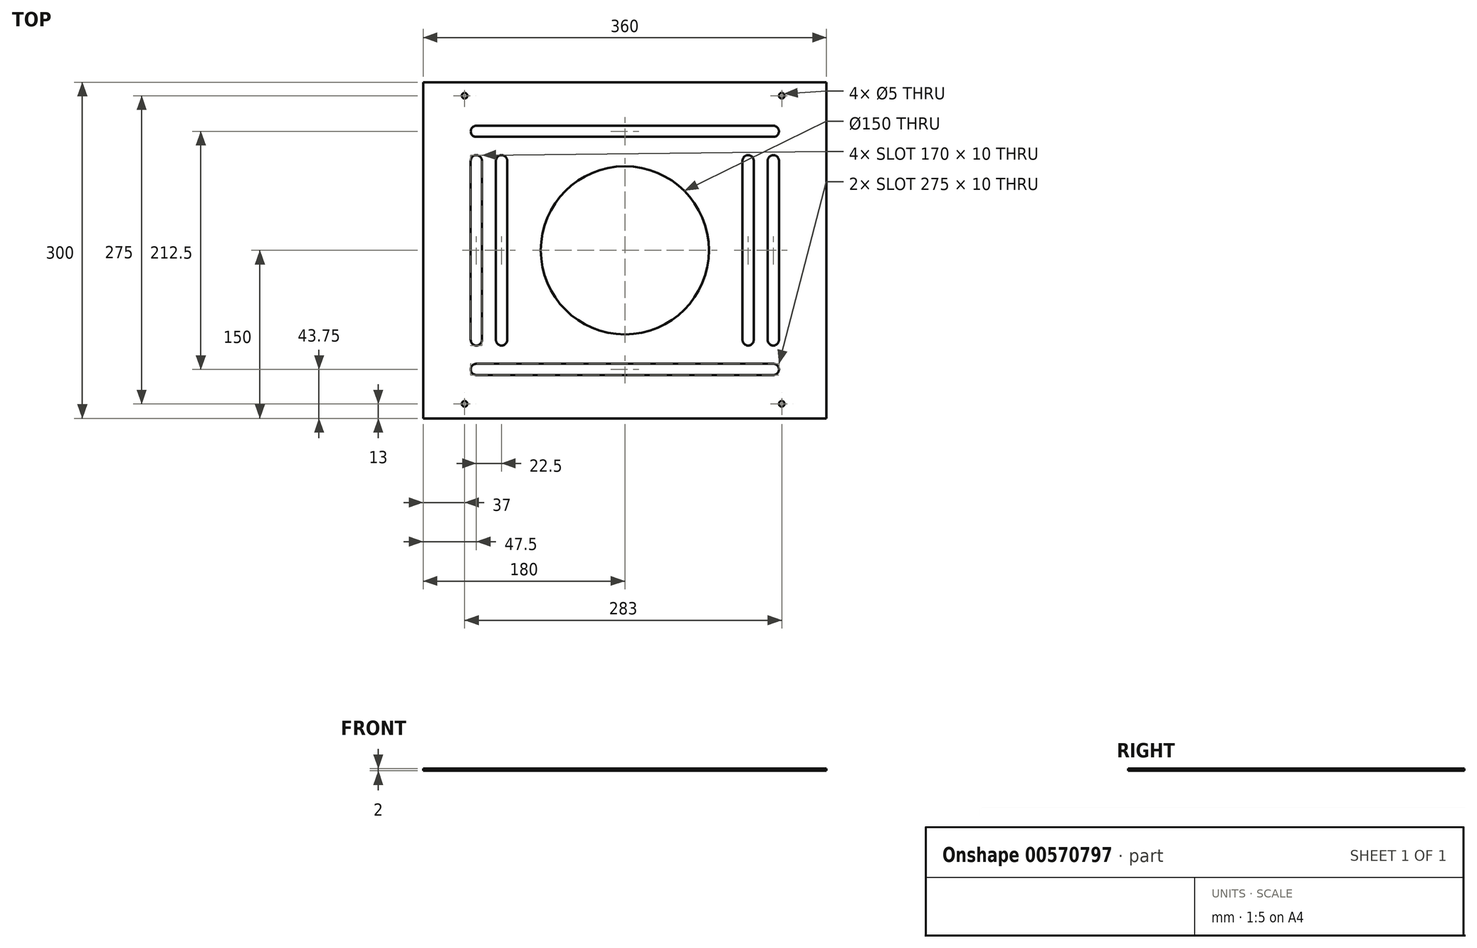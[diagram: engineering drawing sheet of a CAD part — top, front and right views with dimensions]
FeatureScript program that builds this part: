
annotation { "Feature Type Name" : "Feature", "Feature Type Description" : "" }
export const myFeature = defineFeature(function(context is Context, id is Id, definition is map)
    precondition{}
    {
        {
            var Q0;
            Q0=qCreatedBy(makeId("Top.planeOp"),FACE);
            var sketch = newSketch(context, id + "F0", { "sketchPlane" : qUnion([Q0])});
            skLineSegment(sketch, "E0.bottom", {"start": v(0, 0) * mm, "end": v(360, 0) * mm});
            skLineSegment(sketch, "E0.top", {"start": v(0, 300) * mm, "end": v(360, 300) * mm});
            skLineSegment(sketch, "E0.left", {"start": v(0, 0) * mm, "end": v(0, 300) * mm});
            skLineSegment(sketch, "E0.right", {"start": v(360, 0) * mm, "end": v(360, 300) * mm});
            skCircle(sketch, "E1", {"center": v(180, 150) * mm, "radius": 75 * mm});
            skPoint(sketch, "E1.centerSnap0", {"position": v(180, 0) * mm});
            skPoint(sketch, "E1.centerSnap1", {"position": v(0, 150) * mm});
            skCircle(sketch, "E2", {"center": v(320, 13) * mm, "radius": 2.5 * mm});
            skCircle(sketch, "E3", {"center": v(37, 13) * mm, "radius": 2.5 * mm});
            skCircle(sketch, "E4", {"center": v(37, 288) * mm, "radius": 2.5 * mm});
            skLineSegment(sketch, "E5.0", {"start": v(25, 275) * mm, "end": v(335, 275) * mm, "construction": true});
            skLineSegment(sketch, "E5.1", {"start": v(25, 25) * mm, "end": v(25, 275) * mm, "construction": true});
            skLineSegment(sketch, "E5.2", {"start": v(25, 25) * mm, "end": v(335, 25) * mm, "construction": true});
            skLineSegment(sketch, "E5.3", {"start": v(335, 25) * mm, "end": v(335, 275) * mm, "construction": true});
            skCircle(sketch, "E6", {"center": v(180, 150) * mm, "radius": 87.5 * mm, "construction": true});
            skLineSegment(sketch, "E7", {"start": v(70, 230) * mm, "end": v(70, 70) * mm, "construction": true});
            skLineSegment(sketch, "E8", {"start": v(0, 150) * mm, "end": v(360, 150) * mm, "construction": true});
            skLineSegment(sketch, "E9", {"start": v(180, 300) * mm, "end": v(180, 0) * mm, "construction": true});
            skLineSegment(sketch, "E10", {"start": v(47.5, 230) * mm, "end": v(47.5, 70) * mm, "construction": true});
            skLineSegment(sketch, "E11", {"start": v(290, 230) * mm, "end": v(290, 70) * mm, "construction": true});
            skLineSegment(sketch, "E12", {"start": v(312.5, 230) * mm, "end": v(312.5, 70) * mm, "construction": true});
            skLineSegment(sketch, "E13", {"start": v(47.5, 256.25) * mm, "end": v(312.5, 256.25) * mm, "construction": true});
            skLineSegment(sketch, "E14", {"start": v(47.5, 43.75) * mm, "end": v(312.5, 43.75) * mm, "construction": true});
            skArc(sketch, "E15.0.startCap", {"start": v(42.5, 230) * mm, "mid": v(47.5, 235) * mm, "end": v(52.5, 230) * mm});
            skArc(sketch, "E15.0.endCap", {"start": v(52.5, 70) * mm, "mid": v(47.5, 65) * mm, "end": v(42.5, 70) * mm});
            skLineSegment(sketch, "E15.0.left", {"start": v(52.5, 230) * mm, "end": v(52.5, 70) * mm});
            skLineSegment(sketch, "E15.0.right", {"start": v(42.5, 230) * mm, "end": v(42.5, 70) * mm});
            skArc(sketch, "E15.1.startCap", {"start": v(65, 230) * mm, "mid": v(70, 235) * mm, "end": v(75, 230) * mm});
            skArc(sketch, "E15.1.endCap", {"start": v(75, 70) * mm, "mid": v(70, 65) * mm, "end": v(65, 70) * mm});
            skLineSegment(sketch, "E15.1.left", {"start": v(75, 230) * mm, "end": v(75, 70) * mm});
            skLineSegment(sketch, "E15.1.right", {"start": v(65, 230) * mm, "end": v(65, 70) * mm});
            skArc(sketch, "E15.2.startCap", {"start": v(47.5, 38.75) * mm, "mid": v(42.5, 43.75) * mm, "end": v(47.5, 48.75) * mm});
            skArc(sketch, "E15.2.endCap", {"start": v(312.5, 48.75) * mm, "mid": v(317.5, 43.75) * mm, "end": v(312.5, 38.75) * mm});
            skLineSegment(sketch, "E15.2.left", {"start": v(47.5, 48.75) * mm, "end": v(312.5, 48.75) * mm});
            skLineSegment(sketch, "E15.2.right", {"start": v(47.5, 38.75) * mm, "end": v(312.5, 38.75) * mm});
            skArc(sketch, "E15.3.startCap", {"start": v(47.5, 251.25) * mm, "mid": v(42.5, 256.25) * mm, "end": v(47.5, 261.25) * mm});
            skArc(sketch, "E15.3.endCap", {"start": v(312.5, 261.25) * mm, "mid": v(317.5, 256.25) * mm, "end": v(312.5, 251.25) * mm});
            skLineSegment(sketch, "E15.3.left", {"start": v(47.5, 261.25) * mm, "end": v(312.5, 261.25) * mm});
            skLineSegment(sketch, "E15.3.right", {"start": v(47.5, 251.25) * mm, "end": v(312.5, 251.25) * mm});
            skArc(sketch, "E15.4.startCap", {"start": v(285, 230) * mm, "mid": v(290, 235) * mm, "end": v(295, 230) * mm});
            skArc(sketch, "E15.4.endCap", {"start": v(295, 70) * mm, "mid": v(290, 65) * mm, "end": v(285, 70) * mm});
            skLineSegment(sketch, "E15.4.left", {"start": v(295, 230) * mm, "end": v(295, 70) * mm});
            skLineSegment(sketch, "E15.4.right", {"start": v(285, 230) * mm, "end": v(285, 70) * mm});
            skArc(sketch, "E15.5.startCap", {"start": v(307.5, 230) * mm, "mid": v(312.5, 235) * mm, "end": v(317.5, 230) * mm});
            skArc(sketch, "E15.5.endCap", {"start": v(317.5, 70) * mm, "mid": v(312.5, 65) * mm, "end": v(307.5, 70) * mm});
            skLineSegment(sketch, "E15.5.left", {"start": v(317.5, 230) * mm, "end": v(317.5, 70) * mm});
            skLineSegment(sketch, "E15.5.right", {"start": v(307.5, 230) * mm, "end": v(307.5, 70) * mm});
            skCircle(sketch, "E16", {"center": v(320, 288) * mm, "radius": 2.5 * mm});
            skSolve(sketch);
        }
        {
            var Q0;
            Q0=makeQuery(id+"F0.imprint","IMPRINT",FACE,{"disambiguationData":[TD([[makeQuery(id+"F0.imprint","IMPRINT",EDGE,{"derivedFrom":sQuery(id+"F0.wireOp",EDGE,"E0.bottom")}),1.0]])]});
            extrude(context, id + "F1", {"entities" : qUnion([Q0]), "depth" : 2 * mm, "offsetDistance" : 25 * mm});
        }
    });
